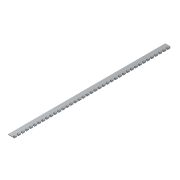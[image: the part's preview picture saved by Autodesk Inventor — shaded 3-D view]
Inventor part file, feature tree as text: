
AUTODESK INVENTOR PART (.ipt)
format: ipt  version: 2012 (Build 160160000, 160)  size: 206,336 bytes
history: native  units: in
note: dims shown in document units (in); Inventor stores cm internally (conversion verified against a paired STEP export)
features: extrude x2, sketch x2, pattern_linear x1
ambient origin geometry x8: Origin, YZ Plane, XZ Plane, XY Plane, X Axis, Y Axis, Z Axis, Center Point
bodies: Solid1 (feature_tree)
feature tree (5):
  extrude  "Extrusion1"  Depth=1.5in
  extrude  "Extrusion2"  Depth=0.25in
  pattern_linear  "Rectangular Pattern1"  Spacing1=39.0in  [1 undecoded]
  sketch  "Sketch1"  dims[d0=0.25in d1=1.5in]
  sketch  "Sketch2"  dims[d2=0.125in d3=0.25in d4=39.0in d5=0.0in d6=0.5in d7=0.5in d8=1.25in d9=1.25in d10=39.0in d11=0.0in d12=15.3543in d14=1.0in]
note: 1 required parameter value undecoded (feature->parameter linkage not recoverable at this tier; creation-order binding heuristic only, values carry confidence <= 0.55)
